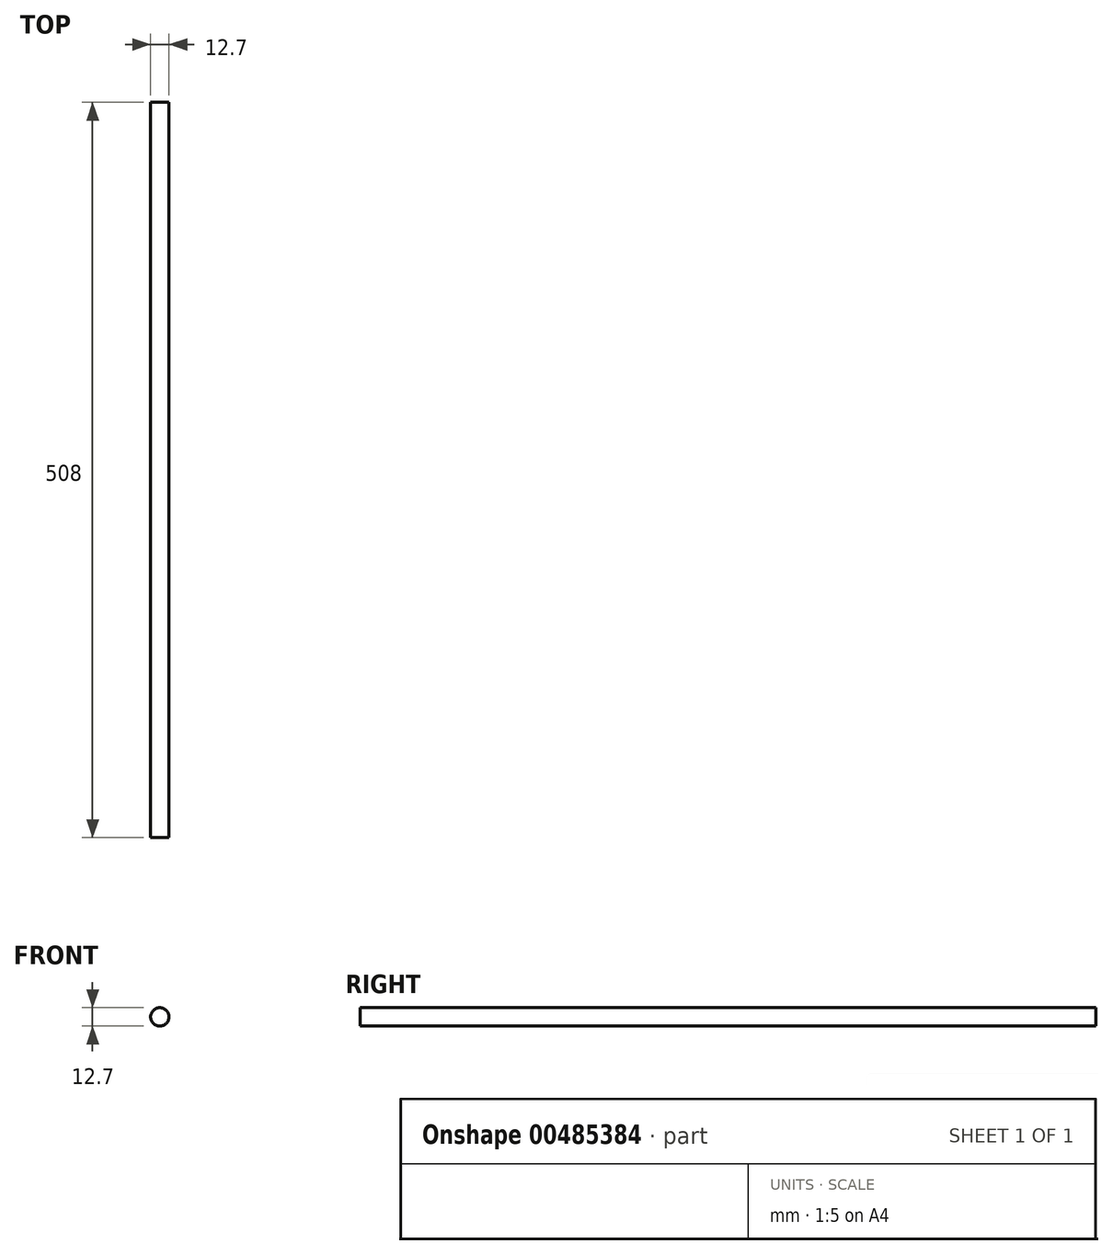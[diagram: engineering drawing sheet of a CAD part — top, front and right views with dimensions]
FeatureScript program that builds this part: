
annotation { "Feature Type Name" : "Feature", "Feature Type Description" : "" }
export const myFeature = defineFeature(function(context is Context, id is Id, definition is map)
    precondition{}
    {
        {
            var Q0;
            Q0=qCreatedBy(makeId("Front.planeOp"),FACE);
            var sketch = newSketch(context, id + "F0", { "sketchPlane" : qUnion([Q0])});
            skCircle(sketch, "E0", {"center": v(0, 0) * mm, "radius": 6.35 * mm});
            skSolve(sketch);
        }
        {
            var Q0;
            Q0=sQuery(id+"F0.wireOp",EDGE,"E0");
            extrude(context, id + "F1", {"bodyType" : ToolBodyType.SURFACE, "surfaceEntities" : qUnion([Q0]), "depth" : 254 * mm, "hasSecondDirection" : true, "secondDirectionOppositeDirection" : true, "secondDirectionDepth" : 254 * mm});
        }
    });
